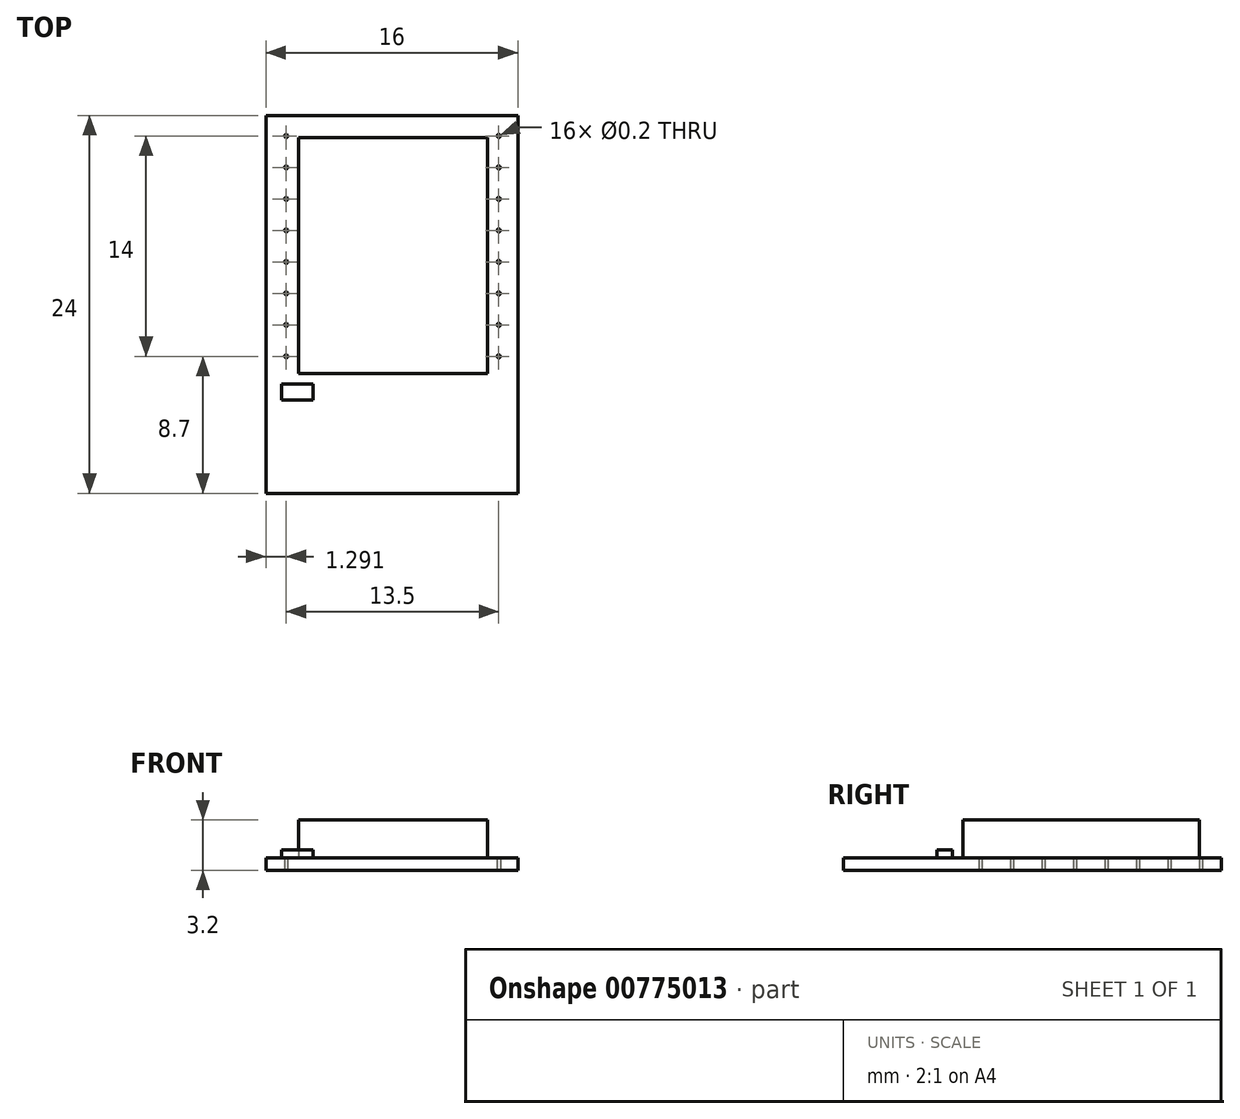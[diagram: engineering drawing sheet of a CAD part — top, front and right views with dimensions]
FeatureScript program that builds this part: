
annotation { "Feature Type Name" : "Feature", "Feature Type Description" : "" }
export const myFeature = defineFeature(function(context is Context, id is Id, definition is map)
    precondition{}
    {
        {
            var Q0;
            Q0=qCreatedBy(makeId("Top.planeOp"),FACE);
            var sketch = newSketch(context, id + "F0", { "sketchPlane" : qUnion([Q0])});
            skLineSegment(sketch, "E0.bottom", {"start": v(-16.27, 7.2) * mm, "end": v(-0.27, 7.2) * mm});
            skLineSegment(sketch, "E0.top", {"start": v(-16.27, -16.8) * mm, "end": v(-0.27, -16.8) * mm});
            skLineSegment(sketch, "E0.left", {"start": v(-16.27, 7.2) * mm, "end": v(-16.27, -16.8) * mm});
            skLineSegment(sketch, "E0.right", {"start": v(-0.27, 7.2) * mm, "end": v(-0.27, -16.8) * mm});
            skCircle(sketch, "E1", {"center": v(-14.98, 5.9) * mm, "radius": 0.1 * mm});
            skCircle(sketch, "E2", {"center": v(-1.48, 5.9) * mm, "radius": 0.1 * mm});
            skCircle(sketch, "E3", {"center": v(-14.98, 3.9) * mm, "radius": 0.1 * mm});
            skCircle(sketch, "E4", {"center": v(-14.98, 1.9) * mm, "radius": 0.1 * mm});
            skCircle(sketch, "E5", {"center": v(-14.98, -0.1) * mm, "radius": 0.1 * mm});
            skCircle(sketch, "E6", {"center": v(-14.98, -2.1) * mm, "radius": 0.1 * mm});
            skCircle(sketch, "E7", {"center": v(-14.98, -4.1) * mm, "radius": 0.1 * mm});
            skCircle(sketch, "E8", {"center": v(-14.98, -6.1) * mm, "radius": 0.1 * mm});
            skCircle(sketch, "E9", {"center": v(-14.98, -8.1) * mm, "radius": 0.1 * mm});
            skCircle(sketch, "E10", {"center": v(-1.48, 3.9) * mm, "radius": 0.1 * mm});
            skCircle(sketch, "E11", {"center": v(-1.48, 1.9) * mm, "radius": 0.1 * mm});
            skCircle(sketch, "E12", {"center": v(-1.48, -0.1) * mm, "radius": 0.1 * mm});
            skCircle(sketch, "E13", {"center": v(-1.48, -2.1) * mm, "radius": 0.1 * mm});
            skCircle(sketch, "E14", {"center": v(-1.48, -4.1) * mm, "radius": 0.1 * mm});
            skCircle(sketch, "E15", {"center": v(-1.48, -6.1) * mm, "radius": 0.1 * mm});
            skCircle(sketch, "E16", {"center": v(-1.48, -8.1) * mm, "radius": 0.1 * mm});
            skLineSegment(sketch, "E17", {"start": v(-14.98, 5.9) * mm, "end": v(-14.98, 3.9) * mm, "construction": true});
            skLineSegment(sketch, "E18", {"start": v(-14.98, 3.9) * mm, "end": v(-14.98, 1.9) * mm, "construction": true});
            skLineSegment(sketch, "E19", {"start": v(-14.98, 1.9) * mm, "end": v(-14.98, -0.1) * mm, "construction": true});
            skLineSegment(sketch, "E20", {"start": v(-14.98, -0.1) * mm, "end": v(-14.98, -2.1) * mm, "construction": true});
            skLineSegment(sketch, "E21", {"start": v(-14.98, -2.1) * mm, "end": v(-14.98, -4.1) * mm, "construction": true});
            skLineSegment(sketch, "E22", {"start": v(-14.98, -4.1) * mm, "end": v(-14.98, -6.1) * mm, "construction": true});
            skLineSegment(sketch, "E23", {"start": v(-14.98, -6.1) * mm, "end": v(-14.98, -8.1) * mm, "construction": true});
            skLineSegment(sketch, "E24", {"start": v(-1.48, 5.9) * mm, "end": v(-1.48, 3.9) * mm, "construction": true});
            skLineSegment(sketch, "E25", {"start": v(-1.48, 3.9) * mm, "end": v(-1.48, 1.9) * mm, "construction": true});
            skLineSegment(sketch, "E26", {"start": v(-1.48, 1.9) * mm, "end": v(-1.48, -0.1) * mm, "construction": true});
            skLineSegment(sketch, "E27", {"start": v(-1.48, -0.1) * mm, "end": v(-1.48, -2.1) * mm, "construction": true});
            skLineSegment(sketch, "E28", {"start": v(-1.48, -2.1) * mm, "end": v(-1.48, -4.1) * mm, "construction": true});
            skLineSegment(sketch, "E29", {"start": v(-1.48, -4.1) * mm, "end": v(-1.48, -6.1) * mm, "construction": true});
            skLineSegment(sketch, "E30", {"start": v(-1.48, -6.1) * mm, "end": v(-1.48, -8.1) * mm, "construction": true});
            skLineSegment(sketch, "E31", {"start": v(-1.48, 5.9) * mm, "end": v(-14.98, 5.9) * mm, "construction": true});
            skSolve(sketch);
        }
        {
            var Q0;
            Q0=makeQuery(id+"F0.imprint","IMPRINT",FACE,{"disambiguationData":[TD([[makeQuery(id+"F0.imprint","IMPRINT",EDGE,{"derivedFrom":sQuery(id+"F0.wireOp",EDGE,"E0.bottom")}),-1.0]])]});
            extrude(context, id + "F1", {"entities" : qUnion([Q0]), "depth" : 0.8 * mm, "offsetDistance" : 25 * mm});
        }
        {
            var Q0;
            Q0=makeQuery(id+"F1.opExtrude","CAP_FACE",FACE,{"disambiguationData":[OSD([sQuery(id+"F0.wireOp",EDGE,"E0.bottom"),sQuery(id+"F0.wireOp",EDGE,"E0.top"),sQuery(id+"F0.wireOp",EDGE,"E0.left"),sQuery(id+"F0.wireOp",EDGE,"E0.right"),sQuery(id+"F0.wireOp",EDGE,"E1"),sQuery(id+"F0.wireOp",EDGE,"E2"),sQuery(id+"F0.wireOp",EDGE,"E3"),sQuery(id+"F0.wireOp",EDGE,"E4"),sQuery(id+"F0.wireOp",EDGE,"E5"),sQuery(id+"F0.wireOp",EDGE,"E6"),sQuery(id+"F0.wireOp",EDGE,"E7"),sQuery(id+"F0.wireOp",EDGE,"E8"),sQuery(id+"F0.wireOp",EDGE,"E9"),sQuery(id+"F0.wireOp",EDGE,"E10"),sQuery(id+"F0.wireOp",EDGE,"E11"),sQuery(id+"F0.wireOp",EDGE,"E12"),sQuery(id+"F0.wireOp",EDGE,"E13"),sQuery(id+"F0.wireOp",EDGE,"E14"),sQuery(id+"F0.wireOp",EDGE,"E15"),sQuery(id+"F0.wireOp",EDGE,"E16")])],"isStart":false});
            var sketch = newSketch(context, id + "F2", { "sketchPlane" : qUnion([Q0])});
            skLineSegment(sketch, "E32.bottom", {"start": v(-14.2, 5.8) * mm, "end": v(-2.2, 5.8) * mm});
            skLineSegment(sketch, "E32.top", {"start": v(-14.2, -9.2) * mm, "end": v(-2.2, -9.2) * mm});
            skLineSegment(sketch, "E32.left", {"start": v(-14.2, 5.8) * mm, "end": v(-14.2, -9.2) * mm});
            skLineSegment(sketch, "E32.right", {"start": v(-2.2, 5.8) * mm, "end": v(-2.2, -9.2) * mm});
            skSolve(sketch);
        }
        {
            var Q0;
            Q0 = qSketchRegion(id + "F2", true);
            extrude(context, id + "F3", {"entities" : qUnion([Q0]), "depth" : 2.4 * mm, "offsetDistance" : 25 * mm});
        }
        {
            var Q0;
            Q0=makeQuery(id+"F1.opExtrude","CAP_FACE",FACE,{"disambiguationData":[OSD([sQuery(id+"F0.wireOp",EDGE,"E0.bottom"),sQuery(id+"F0.wireOp",EDGE,"E0.top"),sQuery(id+"F0.wireOp",EDGE,"E0.left"),sQuery(id+"F0.wireOp",EDGE,"E0.right"),sQuery(id+"F0.wireOp",EDGE,"E1"),sQuery(id+"F0.wireOp",EDGE,"E2"),sQuery(id+"F0.wireOp",EDGE,"E3"),sQuery(id+"F0.wireOp",EDGE,"E4"),sQuery(id+"F0.wireOp",EDGE,"E5"),sQuery(id+"F0.wireOp",EDGE,"E6"),sQuery(id+"F0.wireOp",EDGE,"E7"),sQuery(id+"F0.wireOp",EDGE,"E8"),sQuery(id+"F0.wireOp",EDGE,"E9"),sQuery(id+"F0.wireOp",EDGE,"E10"),sQuery(id+"F0.wireOp",EDGE,"E11"),sQuery(id+"F0.wireOp",EDGE,"E12"),sQuery(id+"F0.wireOp",EDGE,"E13"),sQuery(id+"F0.wireOp",EDGE,"E14"),sQuery(id+"F0.wireOp",EDGE,"E15"),sQuery(id+"F0.wireOp",EDGE,"E16")])],"isStart":false});
            var sketch = newSketch(context, id + "F4", { "sketchPlane" : qUnion([Q0])});
            skLineSegment(sketch, "E33.bottom", {"start": v(-15.27, -9.87) * mm, "end": v(-13.27, -9.87) * mm});
            skLineSegment(sketch, "E33.top", {"start": v(-15.27, -10.87) * mm, "end": v(-13.27, -10.87) * mm});
            skLineSegment(sketch, "E33.left", {"start": v(-15.27, -9.87) * mm, "end": v(-15.27, -10.87) * mm});
            skLineSegment(sketch, "E33.right", {"start": v(-13.27, -9.87) * mm, "end": v(-13.27, -10.87) * mm});
            skSolve(sketch);
        }
        {
            var Q0;
            Q0=makeQuery(id+"F4.imprint","IMPRINT",FACE,{"disambiguationData":[TD([[makeQuery(id+"F4.imprint","IMPRINT",EDGE,{"derivedFrom":sQuery(id+"F4.wireOp",EDGE,"E33.bottom")}),-1.0]])]});
            extrude(context, id + "F5", {"entities" : qUnion([Q0]), "depth" : 0.5 * mm, "offsetDistance" : 25 * mm});
        }
    });
